# Revit family: 0039351+0039354+0039358 Feilo Sylvania Lighting Fixture START HIGHBAY 6K 19KLM WIDE with BRACKET and PC LAMPSHADE TRANSPARENT
name_source: partatom
category: Lighting Fixtures
revit_build: Autodesk Revit 2017 (Build: 20190507_1515(x64)
units: mm (PartAtom-declared; Revit-internal decimal feet)

## family parameters
Cut with Voids When Loaded = No
Host = Face
Light Source = No
OmniClass Number = 23.80.70.00
OmniClass Title = Lighting
Part Type = Normal
Room Calculation Point = No
Round Connector Dimension = Use Diameter
Shared = No

## types (1)
- 0039351+0039354+0039358 START HIGHBAY 6K 19KLM WIDE with BRACKET and PC LAMPSHADE TRANSPARENT
    Apparent Load = 150 VA
    Assembly Code = D5020200
    AssetType = Fixed
    BracketDistanceInner_FEILO = 274 mm
    BracketHeight_FEILO = 210 mm  [stored 0.688976 ft]
    ClassificationName = Uniclass2015
    ClassificationValue = EF_70_80
    Cost = 0 $
    Default Elevation = 1219 mm
    Description = START HIGHBAY, includes 1 m cables, black aluminium housing, 19500LM, 150W, 130lm/W, 6500K, Driver current: 2140mA, CR80, 60° beam angle, 1-10V dimmable,  IP65, IK08, 50,000 hrs (L70B50), (LxWxH) 296x296x177mm
    DocumentationLiterature = http://www.sylvania-lighting.com
    DurationUnit = hours
    ElectricShockClassification = Class I
    ExpectedLife = 50000
    IfcExportAs = IfcLightFixtureType
    IfcExportType = IfcLightFixtureType
    ImpactProtectionIndex = IK08
    IngressProtection = IP65
    InputNominalFrequency = 50/60 Hz
    InputVoltage = 220-240V~
    Keynote = 16500
    Lamp = LED
    LampColourRenderingIndex = 80
    LampColourTemperature = 6500 K
    LampNominalLuminous = 19500 lm
    LampsType = LED
    LuminousEfficacy = 130 lm/W
    Manufacturer = Feilo Sylvania
    ManufacturerName = Feilo Sylvania
    Material = aluminium alloy housing, polycarbonate diffuser
    Material_1_FEILO = Body-Sylvania-StartHighbay-Black
    Material_2_FEILO = <By Category>
    Material_3_FEILO = <By Category>
    Material_4_FEILO = <By Category>
    Model = START HIGHBAY 6K 19KLM WIDE with BRACKET and PC LAMPSHADE TRANSPARENT
    ModelNumber = 0039351+0039354+0039358
    ModelReference = START HIGHBAY 6K 19KLM WIDE with BRACKET and PC LAMPSHADE TRANSPARENT
    Name = START HIGHBAY 6K 19KLM WIDE with BRACKET and PC LAMPSHADE TRANSPARENT
    NominalDepth = 296 mm
    NominalHeight = 177 mm
    NominalLength = 296 mm
    PowerConsumption = 150 W
    PowerFactor = 0.95
    RadiusBendIn_FEILO = 21 mm
    RadiusBendOut_FEILO = 24 mm  [stored 0.0787402 ft]
    RadiusBracketTop_FEILO = 7 mm  [stored 0.0229659 ft]
    SizeBracketM_FEILO = Yes
    SizeBracketS_FEILO = No
    ThicknessBracketPlate_FEILO = 3 mm  [stored 0.00984252 ft]
    Type Image = <None>
    TypeHead_FEILO = Start LED Highbay Head : 0039351+0039354+0039358 START HIGHBAY 6K 19KLM WIDE with BRACKET and PC LAMPSHADE TRANSPARENT
    TypeName = START HIGHBAY 6K 19KLM WIDE with BRACKET and PC LAMPSHADE TRANSPARENT
    URL = http://www.sylvania-lighting.com
    Voltage = 230 V
    Weight = 3.4 kg

note: [stored X ft] marks values corroborated as IEEE doubles in the binary element streams (Revit-internal decimal feet)

## geometry (parser evidence)
native form markers: Sweep x6
no freeform markers — native parametric forms only
